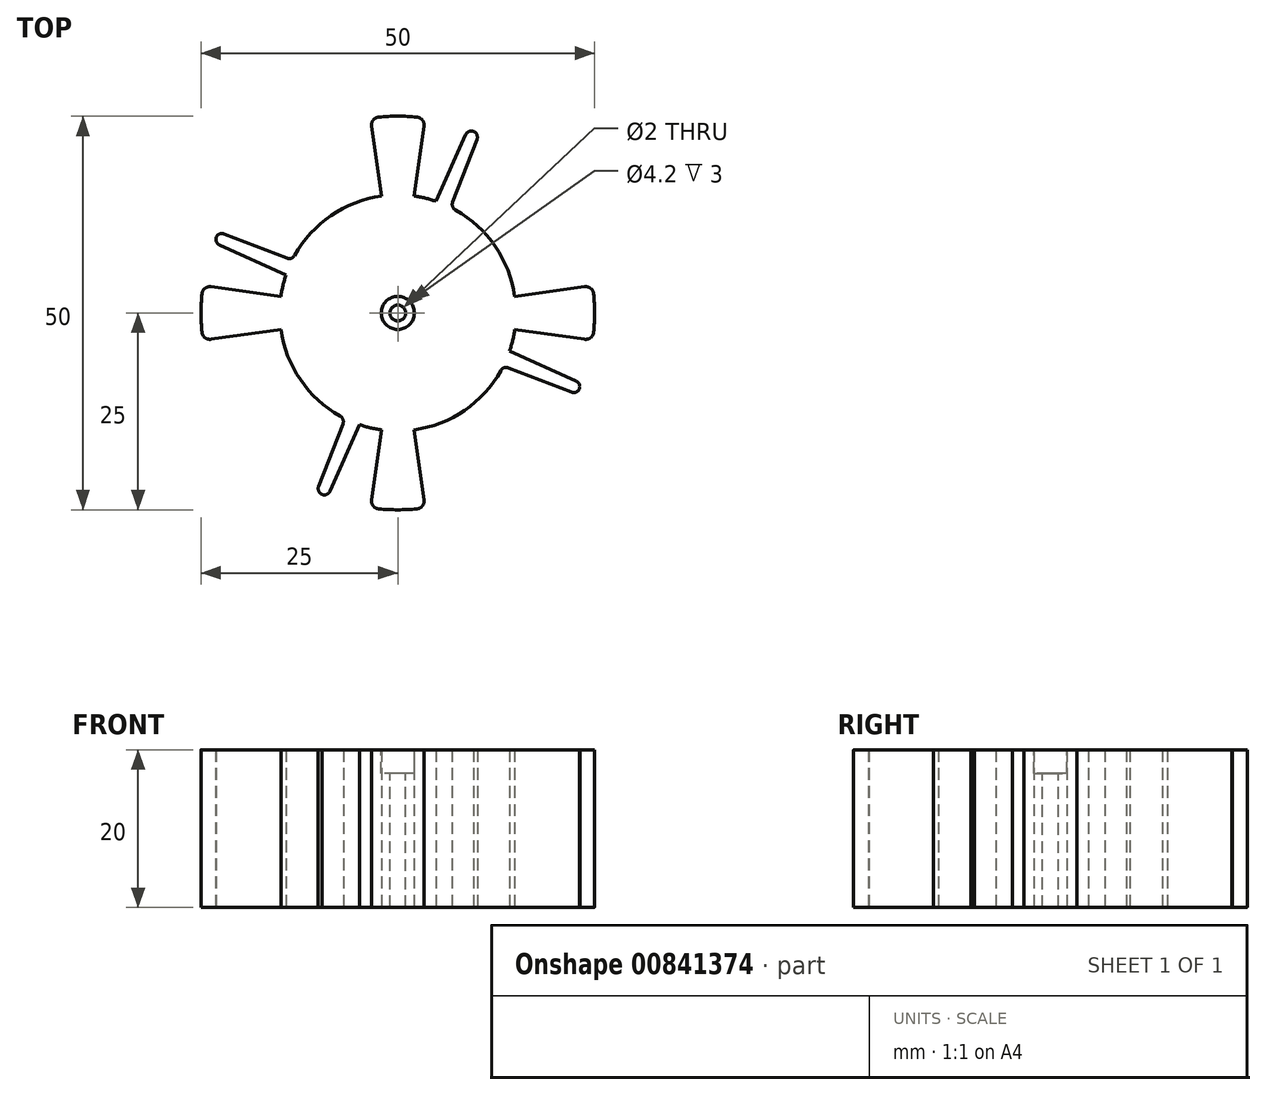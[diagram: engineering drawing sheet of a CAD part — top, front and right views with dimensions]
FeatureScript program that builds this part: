
annotation { "Feature Type Name" : "Feature", "Feature Type Description" : "" }
export const myFeature = defineFeature(function(context is Context, id is Id, definition is map)
    precondition{}
    {
        {
            var Q0;
            Q0=qCreatedBy(makeId("Top.planeOp"),FACE);
            var sketch = newSketch(context, id + "F0", { "sketchPlane" : qUnion([Q0])});
            skCircle(sketch, "E0", {"center": v(0, 0) * mm, "radius": 25 * mm});
            skCircle(sketch, "E1", {"center": v(0, 0) * mm, "radius": 15 * mm});
            skLineSegment(sketch, "E2", {"start": v(-3.48, 24.76) * mm, "end": v(-2.09, 14.85) * mm});
            skLineSegment(sketch, "E3", {"start": v(3.48, 24.76) * mm, "end": v(2.09, 14.85) * mm});
            skLineSegment(sketch, "E4", {"start": v(0, 0) * mm, "end": v(0, 28.73) * mm, "construction": true});
            skLineSegment(sketch, "E5", {"start": v(4.84, 14.2) * mm, "end": v(8.95, 23.34) * mm});
            skLineSegment(sketch, "E6", {"start": v(10.34, 22.76) * mm, "end": v(6.7, 13.42) * mm});
            skLineSegment(sketch, "E7", {"start": v(0, 0) * mm, "end": v(11.66, 27.86) * mm, "construction": true});
            skSolve(sketch);
        }
        {
            var Q0;
            {var subQ0=sQuery(id+"F0.wireOp",EDGE,"E1");var subQ1=makeQuery(id+"F0.imprint","INTERSECT",VERTEX,{"derivedFrom":[subQ0,sQuery(id+"F0.wireOp",EDGE,"E5")]});Q0=makeQuery(id+"F0.imprint","IMPRINT",FACE,{"disambiguationData":[TD([[makeQuery(id+"F0.imprint","IMPRINT",EDGE,{"disambiguationData":[TD([[subQ1,1.0]])],"derivedFrom":subQ0}),1.0]])]});}
            extrude(context, id + "F1", {"entities" : qUnion([Q0]), "depth" : 20 * mm, "offsetDistance" : 25 * mm});
        }
        {
            var Q0;
            {var subQ0=sQuery(id+"F0.wireOp",EDGE,"E2");Q0=makeQuery(id+"F0.imprint","IMPRINT",FACE,{"disambiguationData":[TD([[makeQuery(id+"F0.imprint","IMPRINT",EDGE,{"derivedFrom":subQ0}),1.0]])]});}
            var Q1;
            Q1=makeQuery(id+"F1.opExtrude","CAP_FACE",FACE,{"disambiguationData":[OSD([sQuery(id+"F0.wireOp",EDGE,"E1")])],"isStart":false});
            extrude(context, id + "F2", {"entities" : qUnion([Q0]), "operationType" : NewBodyOperationType.ADD, "endBound" : BoundingType.UP_TO_SURFACE, "depth" : 25 * mm, "endBoundEntityFace" : qUnion([Q1]), "offsetDistance" : 25 * mm});
        }
        {
            var Q0;
            Q0=makeQuery(id+"F2.opExtrude","SWEPT_EDGE",EDGE,{"disambiguationData":[OSD([sQuery(id+"F0.wireOp",EDGE,"E1"),sQuery(id+"F0.wireOp",EDGE,"E2")])]});
            var Q1;
            Q1=makeQuery(id+"F2.opExtrude","SWEPT_EDGE",EDGE,{"disambiguationData":[OSD([sQuery(id+"F0.wireOp",EDGE,"E0"),sQuery(id+"F0.wireOp",EDGE,"E2")])]});
            var Q2;
            Q2=makeQuery(id+"F2.opExtrude","SWEPT_EDGE",EDGE,{"disambiguationData":[OSD([sQuery(id+"F0.wireOp",EDGE,"E0"),sQuery(id+"F0.wireOp",EDGE,"E3")])]});
            var Q3;
            Q3=makeQuery(id+"F2.opExtrude","SWEPT_EDGE",EDGE,{"disambiguationData":[OSD([sQuery(id+"F0.wireOp",EDGE,"E1"),sQuery(id+"F0.wireOp",EDGE,"E3")])]});
            fillet(context, id + "F3", {"entities" : qUnion([Q0, Q1, Q2, Q3]), "radius" : 1 * mm, "tangentPropagation" : true, "allowEdgeOverflow" : false});
        }
        {
            var Q0;
            {var subQ0=sQuery(id+"F0.wireOp",EDGE,"E5");Q0=makeQuery(id+"F0.imprint","IMPRINT",FACE,{"disambiguationData":[TD([[makeQuery(id+"F0.imprint","IMPRINT",EDGE,{"derivedFrom":subQ0}),-1.0]])]});}
            var Q1;
            {var subQ0=sQuery(id+"F0.wireOp",EDGE,"E1");Q1=makeQuery(id+"F2.boolean.opBoolean","MERGE",FACE,{"derivedFrom":[makeQuery(id+"F1.opExtrude","CAP_FACE",FACE,{"disambiguationData":[OSD([subQ0])],"isStart":false}),makeQuery(id+"F2.opExtrude","CAP_FACE",FACE,{"disambiguationData":[OSD([subQ0])],"isStart":false})]});}
            extrude(context, id + "F4", {"entities" : qUnion([Q0]), "operationType" : NewBodyOperationType.ADD, "endBound" : BoundingType.UP_TO_SURFACE, "depth" : 25 * mm, "endBoundEntityFace" : qUnion([Q1]), "offsetDistance" : 25 * mm});
        }
        {
            var Q0;
            Q0=makeQuery(id+"F4.opExtrude","SWEPT_EDGE",EDGE,{"disambiguationData":[OSD([sQuery(id+"F0.wireOp",EDGE,"E0"),sQuery(id+"F0.wireOp",EDGE,"E6")])]});
            var Q1;
            Q1=makeQuery(id+"F4.opExtrude","SWEPT_EDGE",EDGE,{"disambiguationData":[OSD([sQuery(id+"F0.wireOp",EDGE,"E0"),sQuery(id+"F0.wireOp",EDGE,"E5")])]});
            var Q2;
            Q2=makeQuery(id+"F4.opExtrude","SWEPT_EDGE",EDGE,{"disambiguationData":[OSD([sQuery(id+"F0.wireOp",EDGE,"E1"),sQuery(id+"F0.wireOp",EDGE,"E6")])]});
            var Q3;
            Q3=makeQuery(id+"F4.opExtrude","SWEPT_EDGE",EDGE,{"disambiguationData":[OSD([sQuery(id+"F0.wireOp",EDGE,"E1"),sQuery(id+"F0.wireOp",EDGE,"E5")])]});
            fillet(context, id + "F5", {"entities" : qUnion([Q0, Q1, Q2, Q3]), "radius" : 0.8 * mm, "tangentPropagation" : true, "allowEdgeOverflow" : false});
        }
        {
            var Q0;
            Q0=makeQuery(id+"F1.opExtrude","SWEPT_BODY",BODY,{"disambiguationData":[OSD([sQuery(id+"F0.wireOp",EDGE,"E1")])]});
            var Q1;
            {var subQ0=sQuery(id+"F0.wireOp",EDGE,"E6");var subQ2=sQuery(id+"F0.wireOp",EDGE,"E1");Q1=makeQuery(id+"F4x3pG6q38CVNd1_1.3.F4.boolean.opBoolean","SPLIT",FACE,{"disambiguationData":[TD([makeQuery(id+"F4x3pG6q38CVNd1_1.3.F4.opExtrude","SWEPT_FACE",FACE,{"disambiguationData":[OSD([subQ0])]})])],"derivedFrom":makeQuery(id+"F4x3pG6q38CVNd1_1.2.F4.boolean.opBoolean","SPLIT",FACE,{"disambiguationData":[TD([makeQuery(id+"F4x3pG6q38CVNd1_1.2.F4.opExtrude","SWEPT_FACE",FACE,{"disambiguationData":[OSD([subQ0])]})])],"derivedFrom":makeQuery(id+"F4x3pG6q38CVNd1_1.1.F4.boolean.opBoolean","SPLIT",FACE,{"disambiguationData":[TD([makeQuery(id+"F4x3pG6q38CVNd1_1.1.F4.opExtrude","SWEPT_FACE",FACE,{"disambiguationData":[OSD([subQ0])]})])],"derivedFrom":makeQuery(id+"F4.boolean.opBoolean","SPLIT",FACE,{"disambiguationData":[TD([makeQuery(id+"F4.opExtrude","SWEPT_FACE",FACE,{"disambiguationData":[OSD([subQ0])]})])],"derivedFrom":makeQuery(id+"F1.opExtrude","SWEPT_FACE",FACE,{"disambiguationData":[OSD([subQ2])]})})})})});}
            circularPattern(context, id + "F6", {"entities" : qUnion([Q0]), "axis" : qUnion([Q1]), "angle" : 360 * degree, "instanceCount" : 4, "equalSpace" : true});
        }
        {
            var Q0;
            Q0=makeQuery(id+"F1.opExtrude","SWEPT_BODY",BODY,{"disambiguationData":[OSD([sQuery(id+"F0.wireOp",EDGE,"E1")])]});
            var Q1;
            Q1=makeQuery(id+"F6.opPattern","COPY",BODY,{"derivedFrom":makeQuery(id+"F1.opExtrude","SWEPT_BODY",BODY,{"disambiguationData":[OSD([sQuery(id+"F0.wireOp",EDGE,"E1")])]}),"instanceName":"1"});
            var Q2;
            Q2=makeQuery(id+"F6.opPattern","COPY",BODY,{"derivedFrom":makeQuery(id+"F1.opExtrude","SWEPT_BODY",BODY,{"disambiguationData":[OSD([sQuery(id+"F0.wireOp",EDGE,"E1")])]}),"instanceName":"3"});
            var Q3;
            Q3=makeQuery(id+"F6.opPattern","COPY",BODY,{"derivedFrom":makeQuery(id+"F1.opExtrude","SWEPT_BODY",BODY,{"disambiguationData":[OSD([sQuery(id+"F0.wireOp",EDGE,"E1")])]}),"instanceName":"2"});
            booleanBodies(context, id + "F7", {"operationType" : BooleanOperationType.UNION, "tools" : qUnion([Q0, Q1, Q2, Q3])});
        }
        {
            var Q0;
            Q0=qCreatedBy(makeId("Front.planeOp"),FACE);
            var sketch = newSketch(context, id + "F8", { "sketchPlane" : qUnion([Q0])});
            skLineSegment(sketch, "E8", {"start": v(0, 0) * mm, "end": v(0, 20) * mm});
            skLineSegment(sketch, "E9", {"start": v(0, 20) * mm, "end": v(2.1, 20) * mm});
            skLineSegment(sketch, "E10", {"start": v(2.1, 20) * mm, "end": v(2.1, 17) * mm});
            skLineSegment(sketch, "E11", {"start": v(2.1, 17) * mm, "end": v(1, 17) * mm});
            skLineSegment(sketch, "E12", {"start": v(1, 17) * mm, "end": v(1, 0) * mm});
            skLineSegment(sketch, "E13", {"start": v(1, 0) * mm, "end": v(0, 0) * mm});
            skLineSegment(sketch, "E14", {"start": v(0, 0) * mm, "end": v(0, 23.86) * mm, "construction": true});
            skSolve(sketch);
        }
        {
            var Q0;
            Q0 = qSketchRegion(id + "F8", true);
            var Q1;
            Q1=sQuery(id+"F8.wireOp",EDGE,"E14");
            revolve(context, id + "F9", {"operationType" : NewBodyOperationType.REMOVE, "surfaceOperationType" : NewSurfaceOperationType.NEW, "entities" : qUnion([Q0]), "axis" : qUnion([Q1]), "revolveType" : RevolveType.FULL, "oppositeDirection" : true});
        }
    });
